# Revit family: Drain_Floor_Medium-Duty_Zurn-Z540_Sur-Set_Bucket
name_source: partatom
category: Plumbing Fixtures
units: mm (PartAtom-declared; Revit-internal decimal feet)

## family parameters
Always vertical = Yes
Cut with Voids When Loaded = No
Maintain Annotation Orientation = No
OmniClass Number = 23.45.55.21
OmniClass Title = Drains (Wastes)
Part Type = Normal
Room Calculation Point = No
Round Connector Dimension = Use Radius
Shared = No
Work Plane-Based = No

## types (32) — shared parameters
Assembly Code = D2030300
CW Connection = No
Default Elevation = 0' - 4"
Description = 12-1/4 Diameter Top Medium-Duty Drain with Sur-Set Bucket
Grate Open Area (Sq. In) = 18
HW Connection = No
Main Material = Iron - Zurn - Cast - Painted - Blue
Manufacturer = Zurn Water, LLC
Manufacurer Brand = Zurn
Model = Z540
Modified Date = October 28, 2025
Product Documentation Link = https://files.zurn.com
Trap Primer = Yes
URL = www.zurn.com
Vent Connection = No
Waste Connection = Yes
zero-valued in all types: CWFU, HWFU, WFU

## per-type parameters (varying)
| type | E_ Body Height | Frame Height | Outlet Outer Radius | Outlet Radius | Product Installation Sheet URL | Product Page URL | Product data url | Top | Top diameter | Type Comments | ZN-Top |
| ZN541-4NL | 0' - 4 5/8" | 0' - 2 3/16" | 0' - 2 1/4" | 0' - 2" | https://www.zurn.com | https://www.zurn.com | https://www.bimobject.com | Bronze - Zurn - Polished Nickel | 1' - 1" | ZN541-4 Inch Neo-Loc Outlet with Polished Nickel Bronze Top | Yes |
| ZN541-3NL | 0' - 4 5/8" | 0' - 2 3/16" | 0' - 1 3/4" | 0' - 1 1/2" | https://www.zurn.com | https://www.zurn.com | https://www.bimobject.com | Bronze - Zurn - Polished Nickel | 1' - 1" | ZN541-3 Inch Neo-Loc Outlet with Polished Nickel Bronze Top | Yes |
| ZN541-2NL | 0' - 4 5/8" | 0' - 2 3/16" | 0' - 1 3/16" | 0' - 1" | https://www.zurn.com | https://www.zurn.com | https://www.bimobject.com | Bronze - Zurn - Polished Nickel | 1' - 1" | ZN541-2 Inch Neo-Loc Outlet with Polished Nickel Bronze Top | Yes |
| ZN541-8NH | 0' - 5 1/4" | 0' - 2 3/16" | 0' - 4 5/16" | 0' - 4" | https://www.zurn.com | https://www.zurn.com | https://www.bimobject.com | Bronze - Zurn - Polished Nickel | 1' - 1" | ZN541-8 Inch No-Hub Outlet with Polished Nickel Bronze Top | Yes |
| ZN541-6NH | 0' - 5 1/4" | 0' - 2 3/16" | 0' - 3 5/16" | 0' - 3" | https://www.zurn.com | https://www.zurn.com | https://www.bimobject.com | Bronze - Zurn - Polished Nickel | 1' - 1" | ZN541-6 Inch No-Hub Outlet with Polished Nickel Bronze Top | Yes |
| ZN540-4NH Outlet | 0' - 5 1/4" | 0' - 2 3/16" | 0' - 2 1/4" | 0' - 2" | https://files.zurn.com | http://www.zurn.com | https://bimobject.com | Bronze - Zurn - Polished Nickel | 1' - 1" | ZN540-4 Inch No-Hub Outlet with Polished Nickel Bronze Top | Yes |
| ZN541-3NH | 0' - 5 1/4" | 0' - 2 3/16" | 0' - 1 3/4" | 0' - 1 1/2" | https://www.zurn.com | https://www.zurn.com | https://www.bimobject.com | Bronze - Zurn - Polished Nickel | 1' - 1" | ZN541-3 Inch No-Hub Outlet with Polished Nickel Bronze Top | Yes |
| ZN541-2NH | 0' - 5 1/4" | 0' - 2 3/16" | 0' - 1 3/16" | 0' - 1" | https://www.zurn.com | https://www.zurn.com | https://www.bimobject.com | Bronze - Zurn - Polished Nickel | 1' - 1" | ZN541-2 Inch No-Hub Outlet with Polished Nickel Bronze Top | Yes |
| ZN541-8IP | 0' - 3 3/4" | 0' - 2 3/16" | 0' - 4 5/16" | 0' - 4" | https://www.zurn.com | https://www.zurn.com | https://www.bimobject.com | Bronze - Zurn - Polished Nickel | 1' - 1" | ZN541-8 Inch Threaded Outlet with Polished Nickel Bronze Top | Yes |
| ZN541-6IP | 0' - 3 3/4" | 0' - 2 3/16" | 0' - 3 5/16" | 0' - 3" | https://www.zurn.com | https://www.zurn.com | https://www.bimobject.com | Bronze - Zurn - Polished Nickel | 1' - 1" | ZN541-6 Inch Threaded Outlet with Polished Nickel Bronze Top | Yes |
| ZN541-4IP | 0' - 3 3/4" | 0' - 2 3/16" | 0' - 2 1/4" | 0' - 2" | https://www.zurn.com | https://www.zurn.com | https://www.bimobject.com | Bronze - Zurn - Polished Nickel | 1' - 1" | ZN541-4 Inch Threaded Outlet with Polished Nickel Bronze Top | Yes |
| ZN541-3IP | 0' - 3 3/4" | 0' - 2 3/16" | 0' - 1 3/4" | 0' - 1 1/2" | https://www.zurn.com | https://www.zurn.com | https://www.bimobject.com | Bronze - Zurn - Polished Nickel | 1' - 1" | ZN541-3 Inch Threaded Outlet with Polished Nickel Bronze Top | Yes |
| ZN541-2IP | 0' - 3 3/4" | 0' - 2 3/16" | 0' - 1 3/16" | 0' - 1" | https://www.zurn.com | https://www.zurn.com | https://www.bimobject.com | Bronze - Zurn - Polished Nickel | 1' - 1" | ZN541-2 Inch Threaded Outlet with Polished Nickel Bronze Top | Yes |
| ZN541-6IC | 0' - 5 1/4" | 0' - 2 3/16" | 0' - 3 5/16" | 0' - 3" | https://www.zurn.com | https://www.zurn.com | https://www.bimobject.com | Bronze - Zurn - Polished Nickel | 1' - 1" | ZN541-6 Inch Inside Caulk Outlet with Polished Nickel Bronze Top | Yes |
| ZN541-4IC | 0' - 5 1/4" | 0' - 2 3/16" | 0' - 2 1/4" | 0' - 2" | https://www.zurn.com | https://www.zurn.com | https://www.bimobject.com | Bronze - Zurn - Polished Nickel | 1' - 1" | ZN541-4 Inch Inside Caulk Outlet with Polished Nickel Bronze Top | Yes |
| ZN541-3IC | 0' - 5 1/4" | 0' - 2 3/16" | 0' - 1 3/4" | 0' - 1 1/2" | https://www.zurn.com | https://www.zurn.com | https://www.bimobject.com | Bronze - Zurn - Polished Nickel | 1' - 1" | ZN541-3 Inch Inside Caulk Outlet with Polished Nickel Bronze Top | Yes |
| Z541-4NL | 0' - 4 5/8" | 0' - 2" | 0' - 2 1/4" | 0' - 2" | https://www.zurn.com | https://www.zurn.com | https://www.bimobject.com | Iron - Zurn - Cast - Painted - Blue | 1' - 0 1/4" | Z541-4 Inch Neo-Loc Outlet | No |
| Z541-3NL | 0' - 4 5/8" | 0' - 2" | 0' - 1 3/4" | 0' - 1 1/2" | https://www.zurn.com | https://www.zurn.com | https://www.bimobject.com | Iron - Zurn - Cast - Painted - Blue | 1' - 0 1/4" | Z541-3 Inch Neo-Loc Outlet | No |
| Z541-2NL | 0' - 4 5/8" | 0' - 2" | 0' - 1 3/16" | 0' - 1" | https://www.zurn.com | https://www.zurn.com | https://www.bimobject.com | Iron - Zurn - Cast - Painted - Blue | 1' - 0 1/4" | Z541-2 Inch Neo-Loc Outlet | No |
| Z541-8NH | 0' - 5 1/4" | 0' - 2" | 0' - 4 5/16" | 0' - 4" | https://www.zurn.com | https://www.zurn.com | https://www.bimobject.com | Iron - Zurn - Cast - Painted - Blue | 1' - 0 1/4" | Z541-8 Inch No-Hub Outlet | No |
| Z541-6NH | 0' - 5 1/4" | 0' - 2" | 0' - 3 5/16" | 0' - 3" | https://www.zurn.com | https://www.zurn.com | https://www.bimobject.com | Iron - Zurn - Cast - Painted - Blue | 1' - 0 1/4" | Z541-6 Inch No-Hub Outlet | No |
| Z540-4NH Outlet | 0' - 5 1/4" | 0' - 2" | 0' - 2 1/4" | 0' - 2" | https://files.zurn.com | https://www.zurn.com | https://bimobject.com | Iron - Zurn - Cast - Painted - Blue | 1' - 0 1/4" | Z540-4 Inch No-Hub Outlet | No |
| Z541-3NH | 0' - 5 1/4" | 0' - 2" | 0' - 1 3/4" | 0' - 1 1/2" | https://www.zurn.com | https://www.zurn.com | https://www.bimobject.com | Iron - Zurn - Cast - Painted - Blue | 1' - 0 1/4" | Z541-3 Inch No-Hub Outlet | No |
| Z541-2NH | 0' - 5 1/4" | 0' - 2" | 0' - 1 3/16" | 0' - 1" | https://www.zurn.com | https://www.zurn.com | https://www.bimobject.com | Iron - Zurn - Cast - Painted - Blue | 1' - 0 1/4" | Z541-2 Inch No-Hub Outlet | No |
| Z541-8IP | 0' - 3 3/4" | 0' - 2" | 0' - 4 5/16" | 0' - 4" | https://www.zurn.com | https://www.zurn.com | https://www.bimobject.com | Iron - Zurn - Cast - Painted - Blue | 1' - 0 1/4" | Z541-8 Inch Threaded Outlet | No |
| Z541-6IP | 0' - 3 3/4" | 0' - 2" | 0' - 3 5/16" | 0' - 3" | https://www.zurn.com | https://www.zurn.com | https://www.bimobject.com | Iron - Zurn - Cast - Painted - Blue | 1' - 0 1/4" | Z541-6 Inch Threaded Outlet | No |
| Z541-4IP | 0' - 3 3/4" | 0' - 2" | 0' - 2 1/4" | 0' - 2" | https://www.zurn.com | https://www.zurn.com | https://www.bimobject.com | Iron - Zurn - Cast - Painted - Blue | 1' - 0 1/4" | Z541-4 Inch Threaded Outlet | No |
| Z541-3IP | 0' - 3 3/4" | 0' - 2" | 0' - 1 3/4" | 0' - 1 1/2" | https://www.zurn.com | https://www.zurn.com | https://www.bimobject.com | Iron - Zurn - Cast - Painted - Blue | 1' - 0 1/4" | Z541-3 Inch Threaded Outlet | No |
| Z541-2IP | 0' - 3 3/4" | 0' - 2" | 0' - 1 3/16" | 0' - 1" | https://www.zurn.com | https://www.zurn.com | https://www.bimobject.com | Iron - Zurn - Cast - Painted - Blue | 1' - 0 1/4" | Z541-2 Inch Threaded Outlet | No |
| Z541-6IC | 0' - 5 1/4" | 0' - 2" | 0' - 3 5/16" | 0' - 3" | https://www.zurn.com | https://www.zurn.com | https://www.bimobject.com | Iron - Zurn - Cast - Painted - Blue | 1' - 0 1/4" | Z541-6 Inch Inside Caulk Outlet | No |
| Z541-4IC | 0' - 5 1/4" | 0' - 2" | 0' - 2 1/4" | 0' - 2" | https://www.zurn.com | https://www.zurn.com | https://www.bimobject.com | Iron - Zurn - Cast - Painted - Blue | 1' - 0 1/4" | Z541-4 Inch Inside Caulk Outlet | No |
| Z541-3IC | 0' - 5 1/4" | 0' - 2" | 0' - 1 3/4" | 0' - 1 1/2" | https://www.zurn.com | https://www.zurn.com | https://www.bimobject.com | Iron - Zurn - Cast - Painted - Blue | 1' - 0 1/4" | Z541-3 Inch Inside Caulk Outlet | No |

## geometry (parser evidence)
native form markers: Sweep x4
no freeform markers — native parametric forms only
